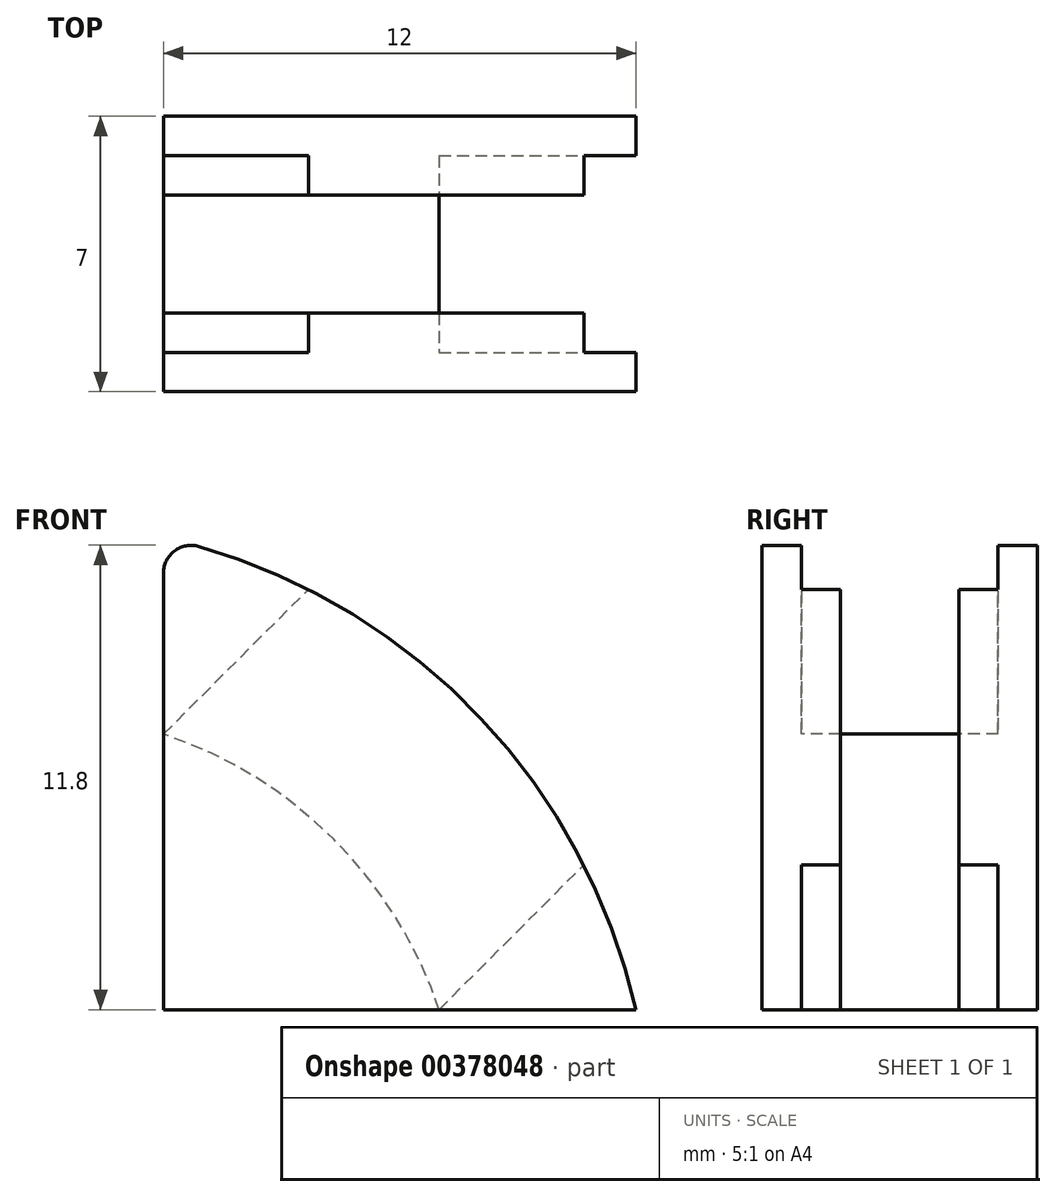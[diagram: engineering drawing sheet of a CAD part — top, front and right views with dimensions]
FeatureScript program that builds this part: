
annotation { "Feature Type Name" : "Feature", "Feature Type Description" : "" }
export const myFeature = defineFeature(function(context is Context, id is Id, definition is map)
    precondition{}
    {
        {
            var Q0;
            Q0=qCreatedBy(makeId("Front.planeOp"),FACE);
            var sketch = newSketch(context, id + "F0", { "sketchPlane" : qUnion([Q0])});
            skLineSegment(sketch, "E0", {"start": v(0, 11.99) * mm, "end": v(0, -11.99) * mm, "construction": true});
            skLineSegment(sketch, "E1", {"start": v(-23, 0) * mm, "end": v(24.7, 0) * mm, "construction": true});
            skLineSegment(sketch, "E2", {"start": v(3.5, 15.5) * mm, "end": v(3.5, 3.5) * mm});
            skLineSegment(sketch, "E3", {"start": v(3.5, 3.5) * mm, "end": v(15.5, 3.5) * mm});
            skArc(sketch, "E4", {"start": v(15.5, 3.5) * mm, "mid": v(11.24, 11.24) * mm, "end": v(3.5, 15.5) * mm});
            skSolve(sketch);
        }
        {
            var Q0;
            Q0 = qSketchRegion(id + "F0", true);
            extrude(context, id + "F1", {"entities" : qUnion([Q0]), "depth" : 7 * mm, "symmetric" : true});
        }
        {
            var Q0;
            Q0=qCreatedBy(makeId("Front.planeOp"),FACE);
            var sketch = newSketch(context, id + "F2", { "sketchPlane" : qUnion([Q0])});
            skArc(sketch, "E5", {"start": v(10.5, 3.5) * mm, "mid": v(7.83, 7.83) * mm, "end": v(3.5, 10.5) * mm});
            skLineSegment(sketch, "E6.0", {"start": v(3.5, 15.5) * mm, "end": v(3.5, 10.5) * mm});
            skLineSegment(sketch, "E7.0", {"start": v(10.5, 3.5) * mm, "end": v(15.5, 3.5) * mm});
            skPoint(sketch, "E8.orphan", {"position": v(3.5, 3.5) * mm});
            skArc(sketch, "E9.0", {"start": v(15.5, 3.5) * mm, "mid": v(11.24, 11.24) * mm, "end": v(3.5, 15.5) * mm});
            skSolve(sketch);
        }
        {
            var Q0;
            Q0 = qSketchRegion(id + "F2", true);
            extrude(context, id + "F3", {"entities" : qUnion([Q0]), "operationType" : NewBodyOperationType.REMOVE, "oppositeDirection" : true, "depth" : 3 * mm, "symmetric" : true});
        }
        {
            var Q0;
            Q0=qCreatedBy(makeId("Front.planeOp"),FACE);
            var sketch = newSketch(context, id + "F4", { "sketchPlane" : qUnion([Q0])});
            skLineSegment(sketch, "E10.0", {"start": v(3.5, 15.5) * mm, "end": v(3.5, 10.5) * mm});
            skLineSegment(sketch, "E11.0", {"start": v(10.5, 3.5) * mm, "end": v(15.5, 3.5) * mm});
            skArc(sketch, "E12.0", {"start": v(15.5, 3.5) * mm, "mid": v(14.95, 5.38) * mm, "end": v(14.18, 7.18) * mm});
            skPoint(sketch, "E13.0", {"position": v(3.5, 10.5) * mm});
            skPoint(sketch, "E14.0", {"position": v(10.5, 3.5) * mm});
            skLineSegment(sketch, "E15", {"start": v(3.5, 10.5) * mm, "end": v(7.18, 14.18) * mm});
            skLineSegment(sketch, "E16", {"start": v(10.5, 3.5) * mm, "end": v(14.18, 7.18) * mm});
            skArc(sketch, "E17.trimOffspring", {"start": v(7.18, 14.18) * mm, "mid": v(5.38, 14.95) * mm, "end": v(3.5, 15.5) * mm});
            skPoint(sketch, "E18.orphan", {"position": v(3.5, 3.5) * mm});
            skSolve(sketch);
        }
        {
            var Q0;
            Q0 = qSketchRegion(id + "F4", true);
            extrude(context, id + "F5", {"entities" : qUnion([Q0]), "operationType" : NewBodyOperationType.REMOVE, "oppositeDirection" : true, "depth" : 5 * mm, "symmetric" : true});
        }
        {
            var Q0;
            {var subQ0=sQuery(id+"F0.wireOp",EDGE,"E2");var subQ1=sQuery(id+"F0.wireOp",EDGE,"E4");Q0=makeQuery(id+"F3.boolean.opBoolean","SPLIT",EDGE,{"disambiguationData":[TD([makeQuery(id+"F1.opExtrude","CAP_FACE",FACE,{"disambiguationData":[OSD([subQ0,sQuery(id+"F0.wireOp",EDGE,"E3"),subQ1])],"isStart":true})])],"derivedFrom":makeQuery(id+"F1.opExtrude","SWEPT_EDGE",EDGE,{"disambiguationData":[OSD([subQ0,subQ1])]})});}
            var Q1;
            {var subQ0=sQuery(id+"F0.wireOp",EDGE,"E2");var subQ1=sQuery(id+"F0.wireOp",EDGE,"E4");Q1=makeQuery(id+"F3.boolean.opBoolean","SPLIT",EDGE,{"disambiguationData":[TD([makeQuery(id+"F1.opExtrude","CAP_FACE",FACE,{"disambiguationData":[OSD([subQ0,sQuery(id+"F0.wireOp",EDGE,"E3"),subQ1])],"isStart":false})])],"derivedFrom":makeQuery(id+"F1.opExtrude","SWEPT_EDGE",EDGE,{"disambiguationData":[OSD([subQ0,subQ1])]})});}
            fillet(context, id + "F6", {"entities" : qUnion([Q0, Q1]), "radius" : 0.7 * mm, "tangentPropagation" : true, "allowEdgeOverflow" : false});
        }
    });
